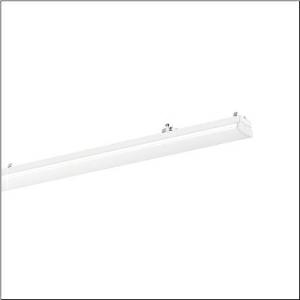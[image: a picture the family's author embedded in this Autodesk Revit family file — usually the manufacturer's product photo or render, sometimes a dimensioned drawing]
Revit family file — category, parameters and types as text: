
# Revit family: licross_r__21_recessed_opal_mo_52tl1dcn485g_66e6
name_source: partatom
category: Lighting Fixtures
units: mm (PartAtom-declared; Revit-internal decimal feet)

## family parameters
Cut with Voids When Loaded = No
Host = Face
Light Source = No
Part Type = Normal
Room Calculation Point = No
Round Connector Dimension = Use Diameter
Shared = No

## types (1)
- --- (1 x LED, 8780 lm, 49.9 W, 4000K)
    Apparent Load = 50 VA
    CIE Flux Codes = 44 73 91 87 100
    Color Rendering = 80
    Color Temperature = 4000K
    Default Elevation = 1800 mm
    Description = Licross® 21 recessed opal MO, luminaire insert, of sheet steel, galvanised, coil coated, white, length: 1.500mm, width: 66mm, height: 67mm, LED rated luminous flux: 8.780lm, light colour: 840, control gear: ON/OFF Multilumen, CLOi, with plug, 3-pole, with phase selection, mains connection: 220..240V, AC, 50/60Hz, start of lifetime: 50W, end of service life: 61W, internal wiring halogen-free, primary optical cover: cover, of PMMA, light emission: direct with ceiling illumination distribution, primary light characteristic: symmetric, protection rating (complete): IP40, insulation class (complete): insulation class I (protective earthing), certification: CE, ENEC, VDE, UKCA, protection symbol: D if used in an environment without relevant dust loads with corresponding accessories, impact resistance: IK06, permissible ambient temperature for indoor applications: -35..+40°C, corresponds to IFS (International Featured Standards) requirements for safety and quality in the food industry, reducing of maximum allowable ambient temperature of 5°C with ceiling mounting, LABS conformity tested according to VDMA 24364:2018-05, packaging unit: 1 piece
    Height = 83 mm
    Lamp = 1 x LED
    Lamp Light Flux = 8780 lm
    Lamp Power = 49.9 W
    Lamp count = 1
    Length = 1500 mm
    Luminous efficacy = 176 lm/W
    Manufacturer = Siteco
    ModVariant = No
    Model = 52TL1DCN485G
    Mounting Place = Ceiling
    Mounting Type = Pendant
    Number of Poles = 1
    OnlyDefault = Yes
    Power Factor = 1
    Product Name = Licross® 21 recessed opal MO
    Product group = luminaire insert | ceiling pendant
    ProductGroupID = 902
    Protection Class = Protection class I
    Protection Degree = IP 40
    RLX_Detail_Level = 1
    RLX_Emergency_Light_Flux = 0 lm
    RLX_Emergency_Type = 0
    RLX_Emergency_Type_DB = No
    RlxData = <blob elided: 24645 chars, md5=fc5a3cbc>
    Socket = socket
    Standby Power = 0 W
    System Light Flux = 8780 lm
    System Power = 50 W
    Type Comments = factory setting: luminous flux: 100 % | (A | C | E) | 116 mA
    Type Image = l_1313666.jpg
    URL = http://relux.com
    VarID = @adj_089677
    Voltage = 0 V
    Weight = 0.00 kg
    Width = 76 mm

## geometry (parser evidence)
native form markers: Blend x4, Sweep x12
no freeform markers — native parametric forms only
